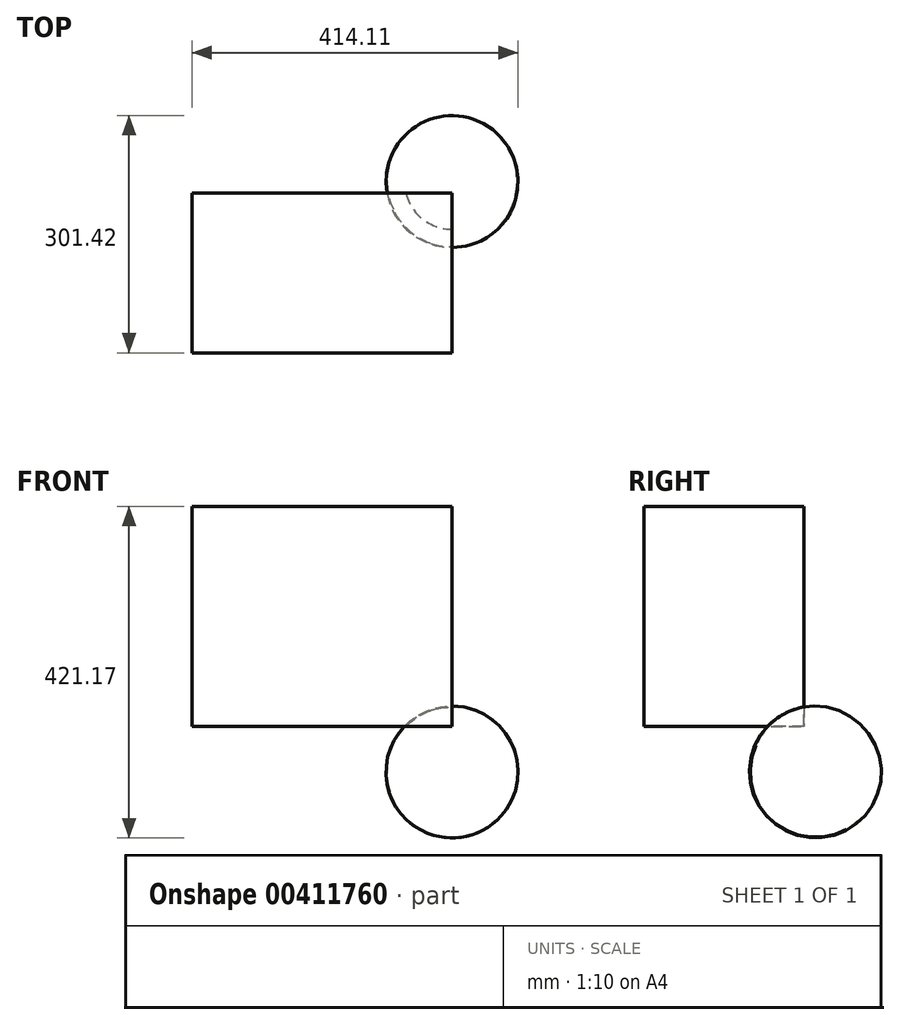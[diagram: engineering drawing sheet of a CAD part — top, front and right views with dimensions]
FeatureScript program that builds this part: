
annotation { "Feature Type Name" : "Feature", "Feature Type Description" : "" }
export const myFeature = defineFeature(function(context is Context, id is Id, definition is map)
    precondition{}
    {
        {
            var Q0;
            Q0=qCreatedBy(makeId("Top.planeOp"),FACE);
            var sketch = newSketch(context, id + "F0", { "sketchPlane" : qUnion([Q0])});
            skLineSegment(sketch, "E0.bottom", {"start": v(-48.39, -46.48) * mm, "end": v(281.81, -46.48) * mm});
            skLineSegment(sketch, "E0.top", {"start": v(-48.39, 156.72) * mm, "end": v(281.81, 156.72) * mm});
            skLineSegment(sketch, "E0.left", {"start": v(-48.39, -46.48) * mm, "end": v(-48.39, 156.72) * mm});
            skLineSegment(sketch, "E0.right", {"start": v(281.81, -46.48) * mm, "end": v(281.81, 156.72) * mm});
            skSolve(sketch);
        }
        {
            var Q0;
            Q0=makeQuery(id+"F0.imprint","IMPRINT",FACE,{"disambiguationData":[TD([[makeQuery(id+"F0.imprint","IMPRINT",EDGE,{"derivedFrom":sQuery(id+"F0.wireOp",EDGE,"E0.bottom")}),1.0]])]});
            extrude(context, id + "F1", {"entities" : qUnion([Q0]), "depth" : 279.4 * mm});
        }
        {
            var Q0;
            Q0=makeQuery(id+"F1.opExtrude","SWEPT_BODY",BODY,{"disambiguationData":[OSD([sQuery(id+"F0.wireOp",EDGE,"E0.bottom"),sQuery(id+"F0.wireOp",EDGE,"E0.top"),sQuery(id+"F0.wireOp",EDGE,"E0.left"),sQuery(id+"F0.wireOp",EDGE,"E0.right")])]});
            transform(context, id + "F2", {"entities" : qUnion([Q0]), "transformType" : TransformType.TRANSLATION_3D, "dx" : 0 * mm, "dy" : 0 * mm, "dz" : 213.36 * mm, "makeCopy" : false});
        }
        {
            var Q0;
            Q0=qCreatedBy(makeId("Right.planeOp"),FACE);
            var Q1;
            Q1=makeQuery(id+"F1.opExtrude","CAP_VERTEX",VERTEX,{"disambiguationData":[OSD([sQuery(id+"F0.wireOp",EDGE,"E0.top"),sQuery(id+"F0.wireOp",EDGE,"E0.right")])],"isStart":true});
            cPlane(context, id + "F3", {"entities" : qUnion([Q0, Q1]), "cplaneType" : CPlaneType.PLANE_POINT, "offset" : 25.4 * mm, "width" : 152.4 * mm, "height" : 152.4 * mm});
        }
        {
            var Q0;
            Q0=qCreatedBy(id+"F3.planeOp",FACE);
            var sketch = newSketch(context, id + "F4", { "sketchPlane" : qUnion([Q0])});
            skLineSegment(sketch, "E1", {"start": v(227.93, 216.34) * mm, "end": v(114.44, 94.28) * mm});
            skArc(sketch, "E2", {"start": v(227.93, 216.34) * mm, "mid": v(109.74, 212.44) * mm, "end": v(114.44, 94.28) * mm});
            skSolve(sketch);
        }
        {
            var Q0;
            Q0=makeQuery(id+"F4.imprint","IMPRINT",FACE,{"disambiguationData":[TD([[makeQuery(id+"F4.imprint","IMPRINT",EDGE,{"derivedFrom":sQuery(id+"F4.wireOp",EDGE,"E1")}),-1.0]])]});
            var Q1;
            Q1=sQuery(id+"F4.wireOp",EDGE,"E1");
            revolve(context, id + "F5", {"operationType" : NewBodyOperationType.ADD, "entities" : qUnion([Q0]), "axis" : qUnion([Q1]), "revolveType" : RevolveType.FULL});
        }
    });
